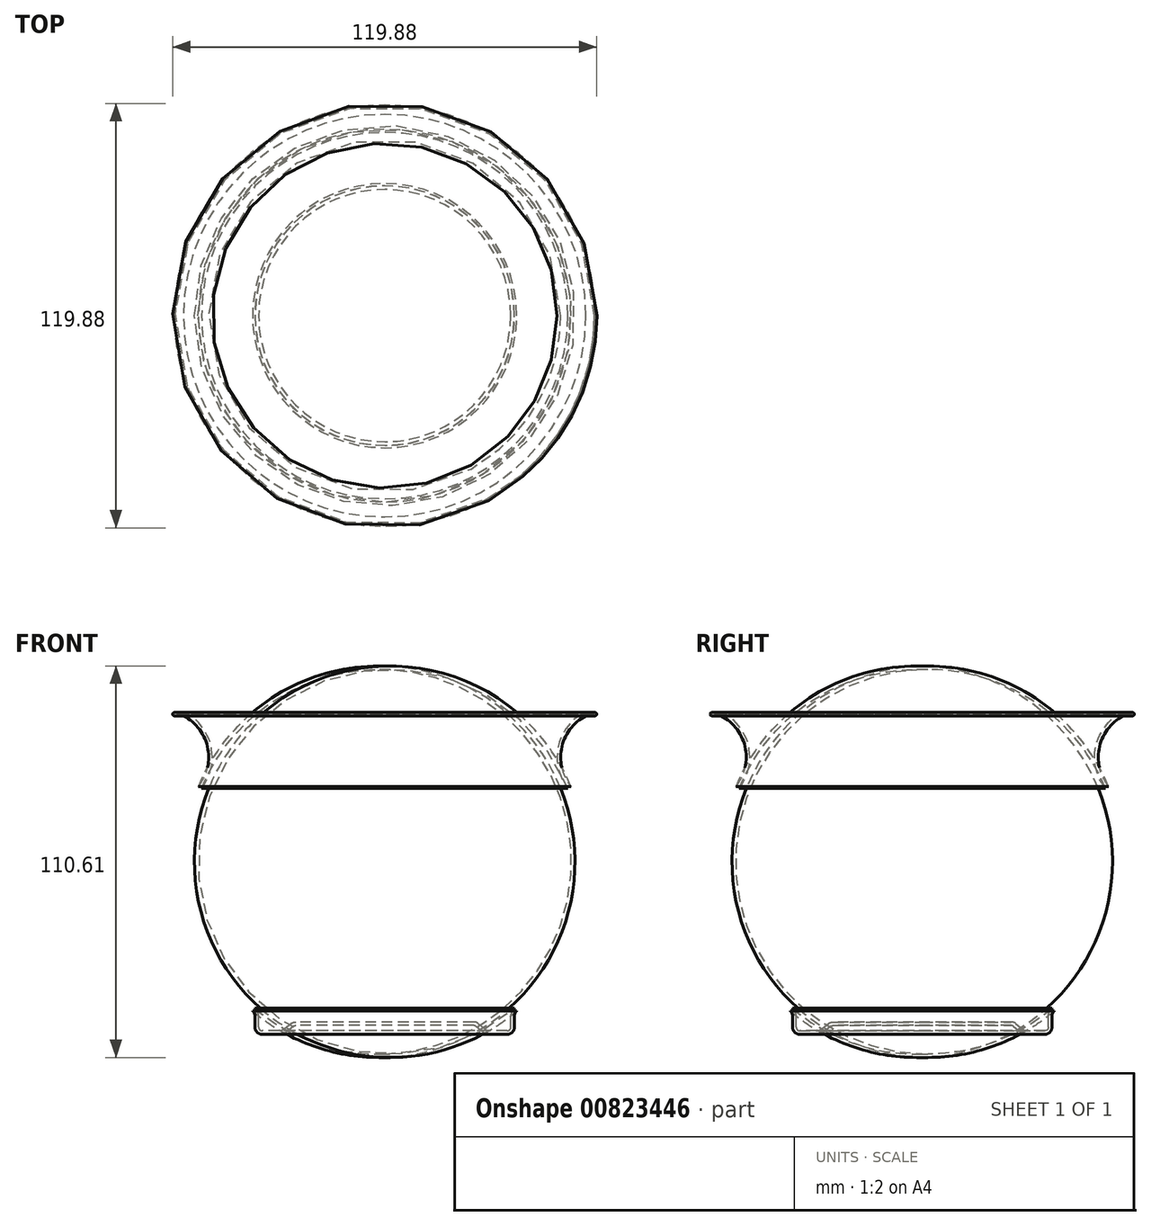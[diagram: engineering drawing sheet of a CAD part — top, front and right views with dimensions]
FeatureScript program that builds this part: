
annotation { "Feature Type Name" : "Feature", "Feature Type Description" : "" }
export const myFeature = defineFeature(function(context is Context, id is Id, definition is map)
    precondition{}
    {
        {
            var Q0;
            Q0=qCreatedBy(makeId("Right.planeOp"),FACE);
            var sketch = newSketch(context, id + "F0", { "sketchPlane" : qUnion([Q0])});
            skLineSegment(sketch, "E0", {"start": v(0, 46.58) * mm, "end": v(0, -48.65) * mm, "construction": true});
            skLineSegment(sketch, "E1", {"start": v(0, 0) * mm, "end": v(25.15, 0) * mm});
            skLineSegment(sketch, "E2", {"start": v(25.77, -0.22) * mm, "end": v(27.8, -1.84) * mm});
            skLineSegment(sketch, "E3", {"start": v(29.68, -2.5) * mm, "end": v(34.62, -2.5) * mm});
            skPoint(sketch, "E4.visualSharp", {"position": v(25.5, 0) * mm});
            skArc(sketch, "E4.filletArc", {"start": v(25.77, -0.22) * mm, "mid": v(25.48, -0.06) * mm, "end": v(25.15, 0) * mm});
            skPoint(sketch, "E5.visualSharp", {"position": v(28.62, -2.5) * mm});
            skArc(sketch, "E5.filletArc", {"start": v(27.8, -1.84) * mm, "mid": v(28.68, -2.33) * mm, "end": v(29.68, -2.5) * mm});
            skLineSegment(sketch, "E6", {"start": v(36.62, -0.5) * mm, "end": v(36.62, 2.56) * mm});
            skPoint(sketch, "E7.visualSharp", {"position": v(36.62, -2.5) * mm});
            skArc(sketch, "E7.filletArc", {"start": v(34.62, -2.5) * mm, "mid": v(36.04, -1.91) * mm, "end": v(36.62, -0.5) * mm});
            skLineSegment(sketch, "E8", {"start": v(52.62, -2.5) * mm, "end": v(52.62, 67.5) * mm, "construction": true});
            skArc(sketch, "E9", {"start": v(37.33, 4.09) * mm, "mid": v(55.32, 33.3) * mm, "end": v(52.62, 67.5) * mm});
            skPoint(sketch, "E10.visualSharp", {"position": v(36.62, 3.5) * mm});
            skArc(sketch, "E10.filletArc", {"start": v(37.33, 4.09) * mm, "mid": v(36.8, 3.4) * mm, "end": v(36.62, 2.56) * mm});
            skArc(sketch, "E11", {"start": v(56.84, 87.5) * mm, "mid": v(50.01, 78.5) * mm, "end": v(52.62, 67.5) * mm});
            skArc(sketch, "E12.0", {"start": v(55.89, 88.12) * mm, "mid": v(49, 78.5) * mm, "end": v(51.75, 66.99) * mm});
            skArc(sketch, "E12.1", {"start": v(36.68, 4.85) * mm, "mid": v(54.33, 33.47) * mm, "end": v(51.75, 66.99) * mm});
            skArc(sketch, "E12.2", {"start": v(36.68, 4.85) * mm, "mid": v(35.9, 3.82) * mm, "end": v(35.62, 2.56) * mm});
            skLineSegment(sketch, "E12.3", {"start": v(35.62, -0.5) * mm, "end": v(35.62, 2.56) * mm});
            skArc(sketch, "E12.4", {"start": v(34.62, -1.5) * mm, "mid": v(35.33, -1.2) * mm, "end": v(35.62, -0.5) * mm});
            skLineSegment(sketch, "E12.5", {"start": v(29.68, -1.5) * mm, "end": v(34.62, -1.5) * mm});
            skLineSegment(sketch, "E12.6", {"start": v(0, 1) * mm, "end": v(25.15, 1) * mm});
            skArc(sketch, "E12.7", {"start": v(26.4, 0.56) * mm, "mid": v(25.81, 0.89) * mm, "end": v(25.15, 1) * mm});
            skLineSegment(sketch, "E12.8", {"start": v(26.4, 0.56) * mm, "end": v(28.43, -1.06) * mm});
            skArc(sketch, "E12.9", {"start": v(28.43, -1.06) * mm, "mid": v(29.01, -1.39) * mm, "end": v(29.68, -1.5) * mm});
            skLineSegment(sketch, "E13", {"start": v(0, 0) * mm, "end": v(0, 1) * mm});
            skLineSegment(sketch, "E14", {"start": v(56.88, 88.39) * mm, "end": v(59.49, 88.39) * mm});
            skArc(sketch, "E15", {"start": v(59.49, 87.48) * mm, "mid": v(59.94, 87.93) * mm, "end": v(59.49, 88.39) * mm});
            skArc(sketch, "E16", {"start": v(59.29, 87.7) * mm, "mid": v(58.05, 87.7) * mm, "end": v(56.84, 87.5) * mm});
            skPoint(sketch, "E17.visualSharp", {"position": v(56.37, 88.39) * mm});
            skArc(sketch, "E17.filletArc", {"start": v(56.88, 88.39) * mm, "mid": v(56.37, 88.32) * mm, "end": v(55.89, 88.12) * mm});
            skArc(sketch, "E18", {"start": v(59.29, 87.7) * mm, "mid": v(59.33, 87.54) * mm, "end": v(59.49, 87.48) * mm});
            skSolve(sketch);
        }
        {
            var Q0;
            Q0=makeQuery(id+"F0.imprint","IMPRINT",FACE,{"disambiguationData":[TD([[makeQuery(id+"F0.imprint","IMPRINT",EDGE,{"derivedFrom":sQuery(id+"F0.wireOp",EDGE,"E1")}),1.0]])]});
            var Q1;
            Q1=sQuery(id+"F0.wireOp",EDGE,"E0");
            revolve(context, id + "F1", {"surfaceOperationType" : NewSurfaceOperationType.NEW, "entities" : qUnion([Q0]), "axis" : qUnion([Q1]), "revolveType" : RevolveType.FULL});
        }
    });
